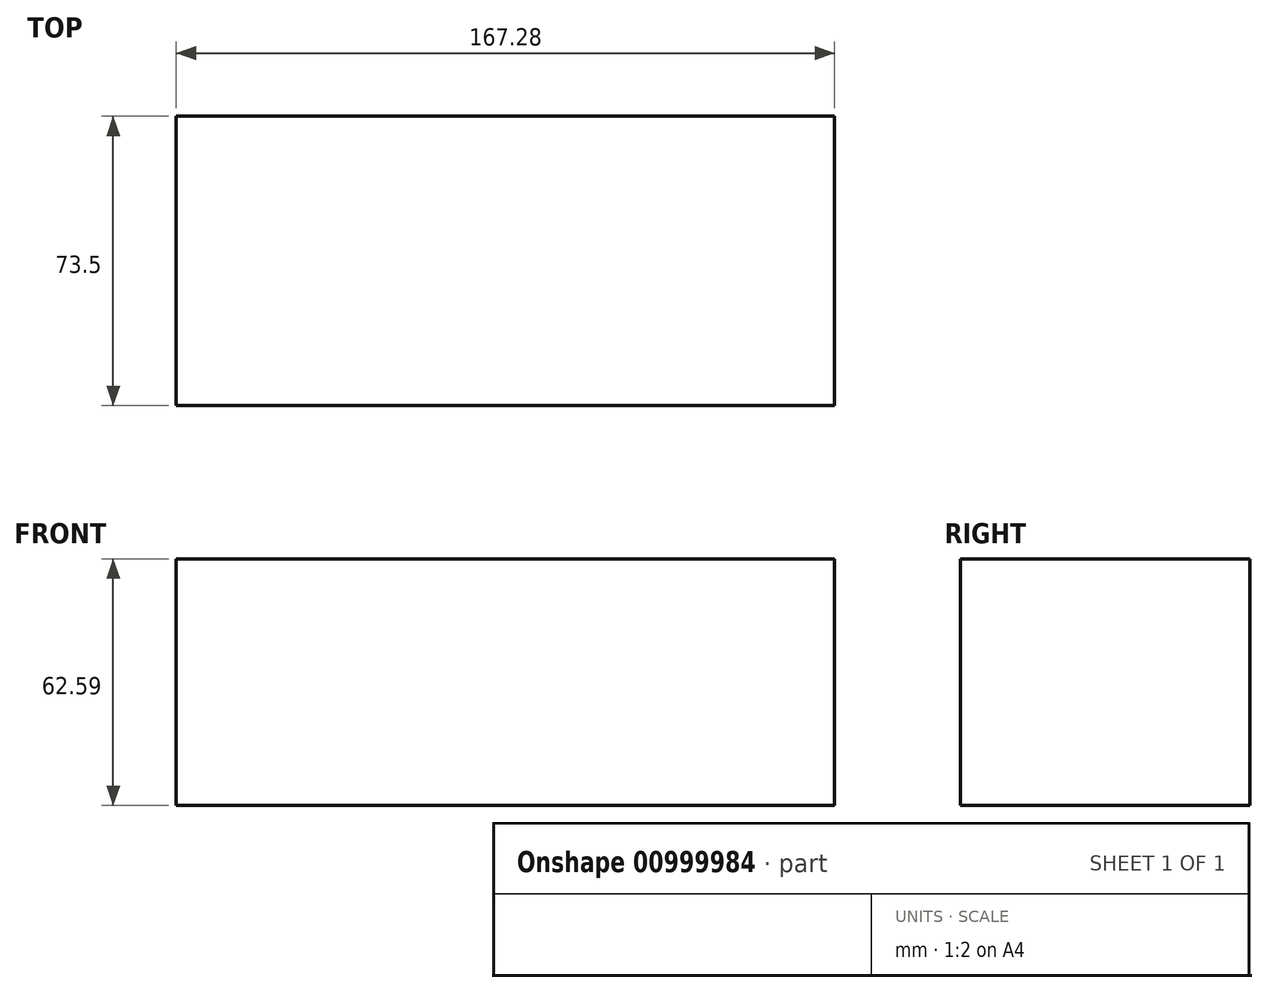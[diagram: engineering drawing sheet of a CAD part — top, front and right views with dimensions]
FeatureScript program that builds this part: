
annotation { "Feature Type Name" : "Feature", "Feature Type Description" : "" }
export const myFeature = defineFeature(function(context is Context, id is Id, definition is map)
    precondition{}
    {
        {
            var Q0;
            Q0=qCreatedBy(makeId("Front.planeOp"),FACE);
            var sketch = newSketch(context, id + "F0", { "sketchPlane" : qUnion([Q0])});
            skLineSegment(sketch, "E0.bottom", {"start": v(-15.4, 32.84) * mm, "end": v(151.88, 32.84) * mm});
            skLineSegment(sketch, "E0.top", {"start": v(-15.4, -29.75) * mm, "end": v(151.88, -29.75) * mm});
            skLineSegment(sketch, "E0.left", {"start": v(-15.4, 32.84) * mm, "end": v(-15.4, -29.75) * mm});
            skLineSegment(sketch, "E0.right", {"start": v(151.88, 32.84) * mm, "end": v(151.88, -29.75) * mm});
            skSolve(sketch);
        }
        {
            var Q0;
            Q0=makeQuery(id+"F0.imprint","IMPRINT",FACE,{"disambiguationData":[TD([[makeQuery(id+"F0.imprint","IMPRINT",EDGE,{"derivedFrom":sQuery(id+"F0.wireOp",EDGE,"E0.bottom")}),-1.0]])]});
            extrude(context, id + "F1", {"entities" : qUnion([Q0]), "depth" : 73.5 * mm, "offsetDistance" : 25 * mm});
        }
    });
